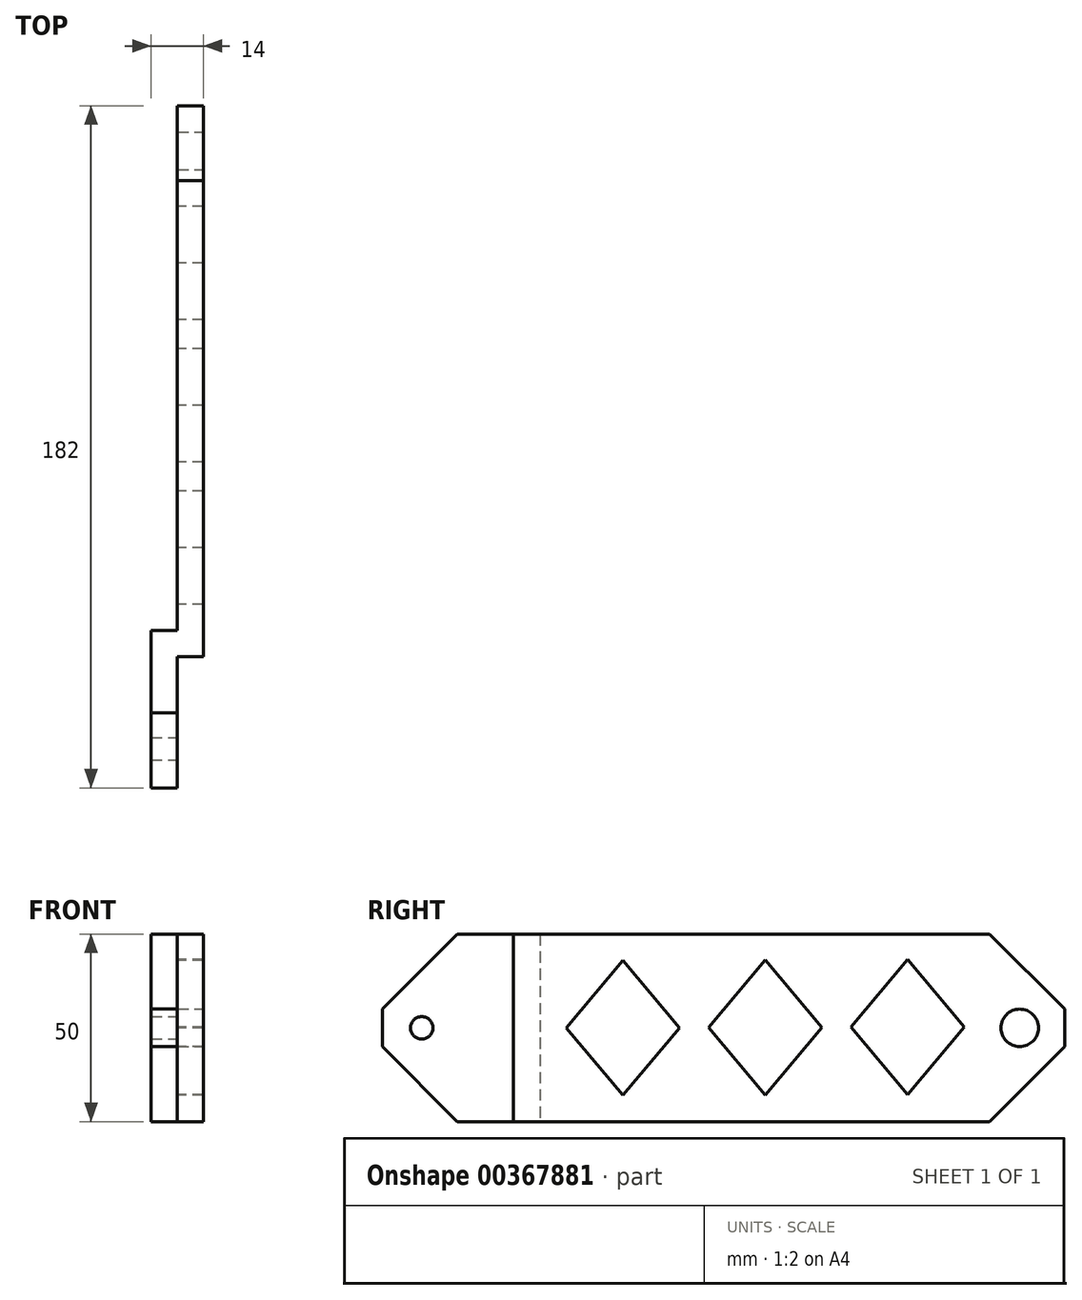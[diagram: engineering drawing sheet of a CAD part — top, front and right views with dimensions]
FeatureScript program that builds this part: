
annotation { "Feature Type Name" : "Feature", "Feature Type Description" : "" }
export const myFeature = defineFeature(function(context is Context, id is Id, definition is map)
    precondition{}
    {
        {
            var Q0;
            Q0=qCreatedBy(makeId("Top.planeOp"),FACE);
            var sketch = newSketch(context, id + "F0", { "sketchPlane" : qUnion([Q0])});
            skLineSegment(sketch, "E0.bottom", {"start": v(-14, -35) * mm, "end": v(-7, -35) * mm});
            skLineSegment(sketch, "E0.left", {"start": v(-14, -35) * mm, "end": v(-14, 7) * mm});
            skLineSegment(sketch, "E0.right", {"start": v(-7, -35) * mm, "end": v(-7, 0) * mm});
            skLineSegment(sketch, "E1.bottom", {"start": v(-14, 7) * mm, "end": v(-7, 7) * mm});
            skLineSegment(sketch, "E1.top", {"start": v(-7, 0) * mm, "end": v(0, 0) * mm});
            skLineSegment(sketch, "E2.top", {"start": v(0, 147) * mm, "end": v(-7, 147) * mm});
            skLineSegment(sketch, "E2.left", {"start": v(0, 0) * mm, "end": v(0, 147) * mm});
            skLineSegment(sketch, "E2.right", {"start": v(-7, 7) * mm, "end": v(-7, 147) * mm});
            skSolve(sketch);
        }
        {
            var Q0;
            Q0=makeQuery(id+"F0.imprint","IMPRINT",FACE,{"disambiguationData":[TD([[makeQuery(id+"F0.imprint","IMPRINT",EDGE,{"derivedFrom":sQuery(id+"F0.wireOp",EDGE,"E0.bottom")}),1.0]])]});
            extrude(context, id + "F1", {"entities" : qUnion([Q0]), "depth" : 50 * mm});
        }
        {
            var Q0;
            Q0=qCreatedBy(makeId("Right.planeOp"),FACE);
            var sketch = newSketch(context, id + "F2", { "sketchPlane" : qUnion([Q0])});
            skCircle(sketch, "E3", {"center": v(135, 25) * mm, "radius": 5 * mm});
            skCircle(sketch, "E4", {"center": v(-24.5, 25) * mm, "radius": 3 * mm});
            skLineSegment(sketch, "E5", {"start": v(-24.5, 25) * mm, "end": v(135, 25) * mm, "construction": true});
            skLineSegment(sketch, "E6", {"start": v(0, 0) * mm, "end": v(0, 50) * mm, "construction": true});
            skSolve(sketch);
        }
        {
            var Q0;
            Q0=makeQuery(id+"F2.imprint","IMPRINT",FACE,{"disambiguationData":[TD([[makeQuery(id+"F2.imprint","IMPRINT",EDGE,{"derivedFrom":sQuery(id+"F2.wireOp",EDGE,"E4")}),1.0]])]});
            var Q1;
            Q1=makeQuery(id+"F2.imprint","IMPRINT",FACE,{"disambiguationData":[TD([[makeQuery(id+"F2.imprint","IMPRINT",EDGE,{"derivedFrom":sQuery(id+"F2.wireOp",EDGE,"E3")}),1.0]])]});
            extrude(context, id + "F3", {"entities" : qUnion([Q0, Q1]), "operationType" : NewBodyOperationType.REMOVE, "oppositeDirection" : true, "depth" : 25 * mm});
        }
        {
            var Q0;
            Q0=makeQuery(id+"F1.opExtrude","SWEPT_FACE",FACE,{"disambiguationData":[OSD([sQuery(id+"F0.wireOp",EDGE,"E2.right")])]});
            var sketch = newSketch(context, id + "F4", { "sketchPlane" : qUnion([Q0])});
            skLineSegment(sketch, "E7", {"start": v(-29.1, 7) * mm, "end": v(-14, 25) * mm});
            skLineSegment(sketch, "E8", {"start": v(-14, 25) * mm, "end": v(-29.1, 43) * mm});
            skLineSegment(sketch, "E9", {"start": v(-29.1, 43) * mm, "end": v(-44.2, 25) * mm});
            skLineSegment(sketch, "E10", {"start": v(-44.2, 25) * mm, "end": v(-29.1, 7) * mm});
            skLineSegment(sketch, "E11", {"start": v(-135, 25) * mm, "end": v(23.96, 25) * mm, "construction": true});
            skPoint(sketch, "E11.endSnap0", {"position": v(-7, 25) * mm});
            skLineSegment(sketch, "E12", {"start": v(-29.1, 43) * mm, "end": v(-29.1, 7) * mm, "construction": true});
            skPoint(sketch, "E13", {"position": v(-29.1, 25) * mm});
            skLineSegment(sketch, "E14.1.0.0", {"start": v(-67.1, 43.1) * mm, "end": v(-82.2, 25.1) * mm});
            skLineSegment(sketch, "E14.1.0.1", {"start": v(-82.2, 25.1) * mm, "end": v(-67.1, 7.1) * mm});
            skLineSegment(sketch, "E14.1.0.2", {"start": v(-52, 25.1) * mm, "end": v(-67.1, 43.1) * mm});
            skLineSegment(sketch, "E14.1.0.3", {"start": v(-67.1, 7.1) * mm, "end": v(-52, 25.1) * mm});
            skLineSegment(sketch, "E14.2.0.0", {"start": v(-105.1, 43.2) * mm, "end": v(-120.2, 25.2) * mm});
            skLineSegment(sketch, "E14.2.0.1", {"start": v(-120.2, 25.2) * mm, "end": v(-105.1, 7.2) * mm});
            skLineSegment(sketch, "E14.2.0.2", {"start": v(-90, 25.2) * mm, "end": v(-105.1, 43.2) * mm});
            skLineSegment(sketch, "E14.2.0.3", {"start": v(-105.1, 7.2) * mm, "end": v(-90, 25.2) * mm});
            skLineSegment(sketch, "E14.direction1", {"start": v(-44.2, 25) * mm, "end": v(-82.2, 25.1) * mm, "construction": true});
            skSolve(sketch);
        }
        {
            var Q0;
            Q0=makeQuery(id+"F4.imprint","IMPRINT",FACE,{"disambiguationData":[TD([[makeQuery(id+"F4.imprint","IMPRINT",EDGE,{"derivedFrom":sQuery(id+"F4.wireOp",EDGE,"E14.2.0.0")}),1.0]])]});
            var Q1;
            Q1=makeQuery(id+"F4.imprint","IMPRINT",FACE,{"disambiguationData":[TD([[makeQuery(id+"F4.imprint","IMPRINT",EDGE,{"derivedFrom":sQuery(id+"F4.wireOp",EDGE,"E14.1.0.0")}),1.0]])]});
            var Q2;
            Q2=makeQuery(id+"F4.imprint","IMPRINT",FACE,{"disambiguationData":[TD([[makeQuery(id+"F4.imprint","IMPRINT",EDGE,{"derivedFrom":sQuery(id+"F4.wireOp",EDGE,"E7")}),1.0]])]});
            extrude(context, id + "F5", {"entities" : qUnion([Q0, Q1, Q2]), "operationType" : NewBodyOperationType.REMOVE, "oppositeDirection" : true, "depth" : 25 * mm});
        }
        {
            var Q0;
            Q0=makeQuery(id+"F1.opExtrude","CAP_EDGE",EDGE,{"disambiguationData":[OSD([sQuery(id+"F0.wireOp",EDGE,"E2.top")])],"isStart":false});
            var Q1;
            Q1=makeQuery(id+"F1.opExtrude","CAP_EDGE",EDGE,{"disambiguationData":[OSD([sQuery(id+"F0.wireOp",EDGE,"E2.top")])],"isStart":true});
            var Q2;
            Q2=makeQuery(id+"F1.opExtrude","CAP_EDGE",EDGE,{"disambiguationData":[OSD([sQuery(id+"F0.wireOp",EDGE,"E0.bottom")])],"isStart":false});
            var Q3;
            Q3=makeQuery(id+"F1.opExtrude","CAP_EDGE",EDGE,{"disambiguationData":[OSD([sQuery(id+"F0.wireOp",EDGE,"E0.bottom")])],"isStart":true});
            chamfer(context, id + "F6", {"entities" : qUnion([Q0, Q1, Q2, Q3]), "chamferType" : ChamferType.OFFSET_ANGLE, "width" : 20 * mm, "oppositeDirection" : true, "angle" : 45 * degree, "tangentPropagation" : true});
        }
    });
